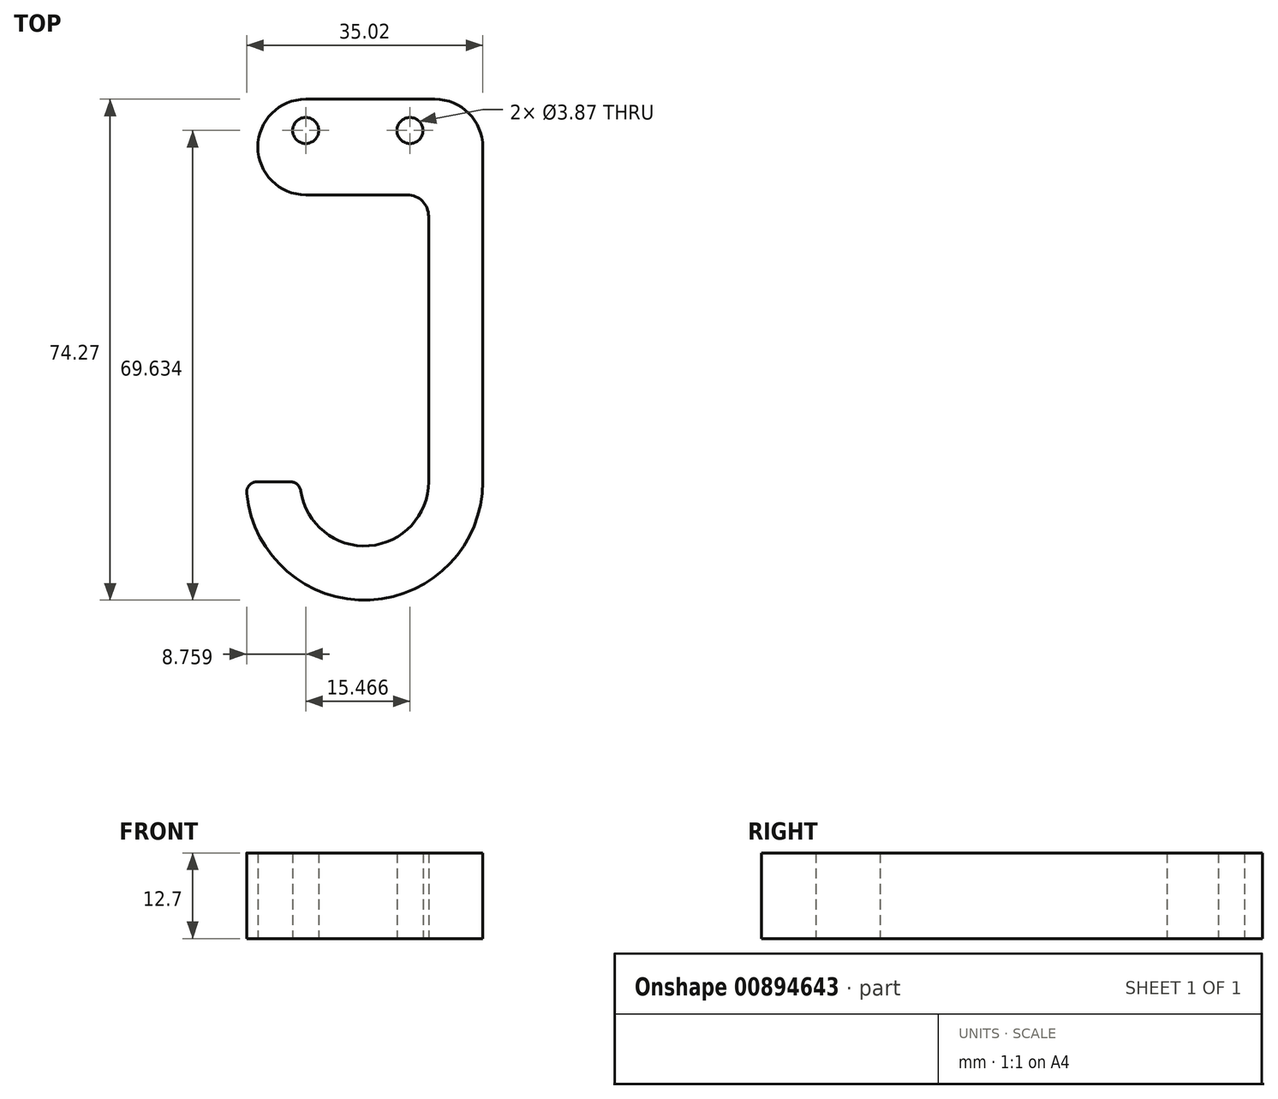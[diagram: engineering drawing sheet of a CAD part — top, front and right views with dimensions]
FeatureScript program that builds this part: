
annotation { "Feature Type Name" : "Feature", "Feature Type Description" : "" }
export const myFeature = defineFeature(function(context is Context, id is Id, definition is map)
    precondition{}
    {
        {
            var Q0;
            Q0=qCreatedBy(makeId("Top.planeOp"),FACE);
            var sketch = newSketch(context, id + "F0", { "sketchPlane" : qUnion([Q0])});
            skArc(sketch, "E0", {"start": v(-17.46, -1.75) * mm, "mid": v(0.87, -17.53) * mm, "end": v(17.55, 0) * mm});
            skLineSegment(sketch, "E1", {"start": v(17.55, 0) * mm, "end": v(17.55, 49.63) * mm});
            skLineSegment(sketch, "E2", {"start": v(10.46, 56.72) * mm, "end": v(-8.71, 56.72) * mm});
            skLineSegment(sketch, "E3", {"start": v(7.1, 42.54) * mm, "end": v(-8.71, 42.54) * mm});
            skLineSegment(sketch, "E4", {"start": v(-15.57, 47.83) * mm, "end": v(-15.57, 47.83) * mm});
            skPoint(sketch, "E5.visualSharp", {"position": v(14.18, 42.54) * mm});
            skPoint(sketch, "E6.visualSharp", {"position": v(17.55, 56.72) * mm});
            skArc(sketch, "E6.filletArc", {"start": v(17.55, 49.63) * mm, "mid": v(15.47, 54.65) * mm, "end": v(10.46, 56.72) * mm});
            skPoint(sketch, "E7.visualSharp", {"position": v(-17.9, 56.72) * mm});
            skArc(sketch, "E7.filletArc", {"start": v(-8.71, 56.72) * mm, "mid": v(-14.33, 53.96) * mm, "end": v(-15.57, 47.83) * mm});
            skPoint(sketch, "E8.visualSharp", {"position": v(-14.18, 42.54) * mm});
            skArc(sketch, "E8.filletArc", {"start": v(-15.57, 47.83) * mm, "mid": v(-13.04, 44.02) * mm, "end": v(-8.71, 42.54) * mm});
            skCircle(sketch, "E9", {"center": v(-8.71, 52.08) * mm, "radius": 1.93 * mm});
            skCircle(sketch, "E10", {"center": v(6.76, 52.08) * mm, "radius": 1.93 * mm});
            skArc(sketch, "E11", {"start": v(-9.43, -1.36) * mm, "mid": v(0.68, -9.5) * mm, "end": v(9.53, 0) * mm});
            skLineSegment(sketch, "E12", {"start": v(9.53, 0) * mm, "end": v(9.53, 39.37) * mm});
            skLineSegment(sketch, "E13", {"start": v(-15.88, 0) * mm, "end": v(-11, 0) * mm});
            skPoint(sketch, "E14.visualSharp", {"position": v(-9.53, 0) * mm});
            skArc(sketch, "E14.filletArc", {"start": v(-9.43, -1.36) * mm, "mid": v(-9.96, -0.39) * mm, "end": v(-11, 0) * mm});
            skArc(sketch, "E15.filletArc", {"start": v(-15.88, 0) * mm, "mid": v(-17.06, -0.52) * mm, "end": v(-17.46, -1.75) * mm});
            skLineSegment(sketch, "E16", {"start": v(6.35, 42.54) * mm, "end": v(7.1, 42.54) * mm});
            skArc(sketch, "E17.filletArc", {"start": v(9.52, 39.37) * mm, "mid": v(8.6, 41.61) * mm, "end": v(6.35, 42.54) * mm});
            skSolve(sketch);
        }
        {
            var Q0;
            Q0=makeQuery(id+"F0.imprint","IMPRINT",FACE,{"disambiguationData":[TD([[makeQuery(id+"F0.imprint","IMPRINT",EDGE,{"derivedFrom":sQuery(id+"F0.wireOp",EDGE,"8fd10817-f83a-4ba5-a682-34303950574c.trimOffspring")}),1.0]])]});
            var Q1;
            Q1=makeQuery(id+"F0.imprint","IMPRINT",FACE,{"disambiguationData":[TD([[makeQuery(id+"F0.imprint","IMPRINT",EDGE,{"derivedFrom":sQuery(id+"F0.wireOp",EDGE,"E0")}),1.0]])]});
            extrude(context, id + "F1", {"entities" : qUnion([Q0, Q1]), "endBound" : BoundingType.SYMMETRIC, "depth" : 12.7 * mm, "offsetDistance" : 25.4 * mm});
        }
    });
